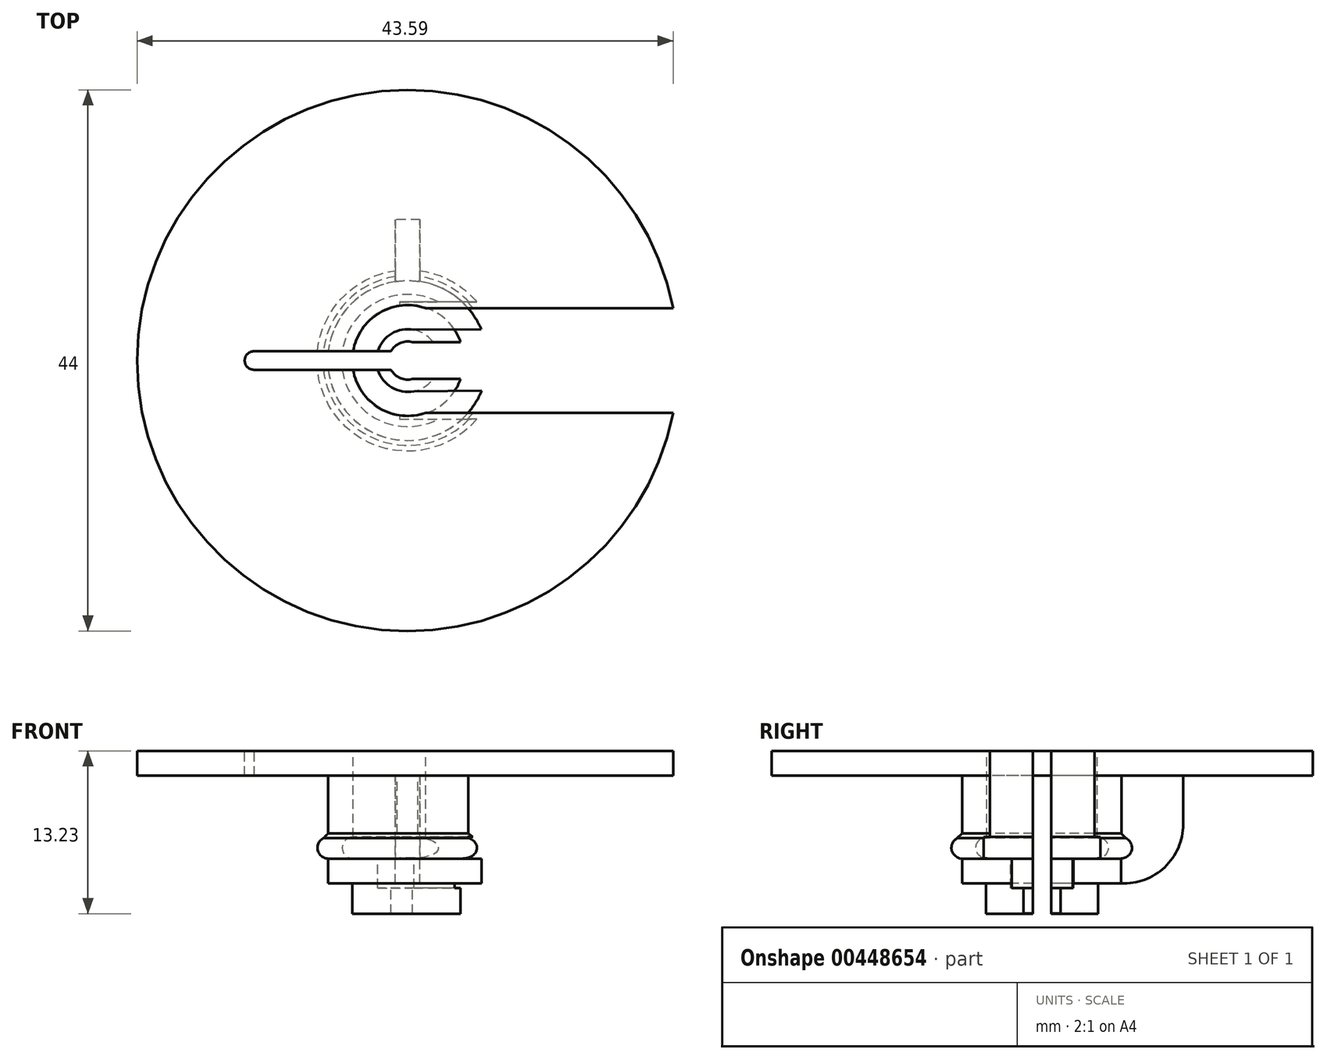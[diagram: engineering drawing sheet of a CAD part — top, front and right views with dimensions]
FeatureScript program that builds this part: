
annotation { "Feature Type Name" : "Feature", "Feature Type Description" : "" }
export const myFeature = defineFeature(function(context is Context, id is Id, definition is map)
    precondition{}
    {
        {
            var Q0;
            Q0=qCreatedBy(makeId("Front.planeOp"),FACE);
            var sketch = newSketch(context, id + "F0", { "sketchPlane" : qUnion([Q0])});
            skLineSegment(sketch, "E0", {"start": v(-22, -6) * mm, "end": v(-22, -8) * mm});
            skLineSegment(sketch, "E1", {"start": v(-22, -8) * mm, "end": v(-6.5, -8) * mm});
            skLineSegment(sketch, "E2", {"start": v(-6.5, -8) * mm, "end": v(-6.5, -12.7) * mm});
            skLineSegment(sketch, "E3", {"start": v(-6.5, -16.75) * mm, "end": v(-4.55, -16.75) * mm});
            skLineSegment(sketch, "E4", {"start": v(-4.55, -16.75) * mm, "end": v(-4.55, -19.23) * mm});
            skLineSegment(sketch, "E5", {"start": v(-22, -6) * mm, "end": v(-4.5, -6) * mm});
            skLineSegment(sketch, "E6", {"start": v(-4.5, -6) * mm, "end": v(-4.5, -13) * mm});
            skLineSegment(sketch, "E7", {"start": v(-4.5, -14.75) * mm, "end": v(-2.55, -14.75) * mm});
            skLineSegment(sketch, "E8", {"start": v(-2.55, -14.75) * mm, "end": v(-2.55, -17.15) * mm});
            skLineSegment(sketch, "E9", {"start": v(-2.55, -19.23) * mm, "end": v(-4.55, -19.23) * mm});
            skArc(sketch, "E10", {"start": v(-4.5, -13) * mm, "mid": v(-5.38, -13.88) * mm, "end": v(-4.5, -14.75) * mm});
            skArc(sketch, "E11", {"start": v(-6.9, -13.1) * mm, "mid": v(-7.35, -14.08) * mm, "end": v(-6.5, -14.75) * mm});
            skLineSegment(sketch, "E12.trimOffspring", {"start": v(-6.5, -14.75) * mm, "end": v(-6.5, -16.75) * mm});
            skLineSegment(sketch, "E13", {"start": v(0, -5.4) * mm, "end": v(0, -17.61) * mm, "construction": true});
            skLineSegment(sketch, "E14", {"start": v(-2.55, -17.15) * mm, "end": v(-1.55, -17.15) * mm});
            skLineSegment(sketch, "E15", {"start": v(-1.55, -17.15) * mm, "end": v(-1.55, -19.22) * mm});
            skLineSegment(sketch, "E16", {"start": v(-1.55, -19.22) * mm, "end": v(-2.55, -19.23) * mm});
            skPoint(sketch, "E17", {"position": v(-5.38, -13.88) * mm});
            skLineSegment(sketch, "E18", {"start": v(-6.9, -13.1) * mm, "end": v(-6.5, -12.7) * mm});
            skSolve(sketch);
        }
        {
            var Q0;
            Q0=makeQuery(id+"F0.imprint","IMPRINT",FACE,{"disambiguationData":[TD([[makeQuery(id+"F0.imprint","IMPRINT",EDGE,{"derivedFrom":sQuery(id+"F0.wireOp",EDGE,"E0")}),1.0]])]});
            var Q1;
            Q1=sQuery(id+"F0.wireOp",EDGE,"E13");
            revolve(context, id + "F1", {"entities" : qUnion([Q0]), "axis" : qUnion([Q1]), "revolveType" : RevolveType.FULL});
        }
        {
            var Q0;
            Q0=makeQuery(id+"F1.opRevolve","SWEPT_FACE",FACE,{"disambiguationData":[OSD([sQuery(id+"F0.wireOp",EDGE,"E5")])]});
            var sketch = newSketch(context, id + "F2", { "sketchPlane" : qUnion([Q0])});
            skLineSegment(sketch, "E19", {"start": v(-1.36, 0.75) * mm, "end": v(-12.48, 0.75) * mm});
            skLineSegment(sketch, "E20", {"start": v(-12.48, -0.75) * mm, "end": v(-1.36, -0.75) * mm});
            skArc(sketch, "E21", {"start": v(-1.36, 0.75) * mm, "mid": v(-1.55, 0) * mm, "end": v(-1.36, -0.75) * mm});
            skArc(sketch, "E22", {"start": v(-12.48, 0.75) * mm, "mid": v(-13.25, 0) * mm, "end": v(-12.48, -0.75) * mm});
            skSolve(sketch);
        }
        {
            var Q0;
            Q0 = qSketchRegion(id + "F2", true);
            extrude(context, id + "F3", {"entities" : qUnion([Q0]), "operationType" : NewBodyOperationType.REMOVE, "endBound" : BoundingType.SYMMETRIC, "oppositeDirection" : true, "depth" : 40 * mm});
        }
        {
            var Q0;
            Q0=makeQuery(id+"F1.opRevolve","SWEPT_FACE",FACE,{"disambiguationData":[OSD([sQuery(id+"F0.wireOp",EDGE,"E5")])]});
            var sketch = newSketch(context, id + "F4", { "sketchPlane" : qUnion([Q0])});
            skLineSegment(sketch, "E23", {"start": v(0, 4.25) * mm, "end": v(0, -4.25) * mm});
            skLineSegment(sketch, "E24", {"start": v(0, -4.25) * mm, "end": v(23.82, -4.25) * mm});
            skLineSegment(sketch, "E25", {"start": v(23.82, -4.25) * mm, "end": v(23.82, 4.25) * mm});
            skLineSegment(sketch, "E26", {"start": v(23.82, 4.25) * mm, "end": v(0, 4.25) * mm});
            skSolve(sketch);
        }
        {
            var Q0;
            Q0 = qSketchRegion(id + "F4", true);
            extrude(context, id + "F5", {"entities" : qUnion([Q0]), "operationType" : NewBodyOperationType.REMOVE, "oppositeDirection" : true, "depth" : 8.4 * mm});
        }
        {
            var Q0;
            {var subQ0=sQuery(id+"F4.wireOp",EDGE,"E24");var subQ2=sQuery(id+"F0.wireOp",EDGE,"E5");var subQ5=makeQuery(id+"F1.opRevolve","SWEPT_EDGE",EDGE,{"disambiguationData":[OSD([sQuery(id+"F0.wireOp",EDGE,"E0"),subQ2])]});var subQ6=makeQuery(id+"F4.imprint","INTERSECT",VERTEX,{"derivedFrom":[subQ5,subQ0]});Q0=makeQuery(id+"F4.imprint","IMPRINT",FACE,{"disambiguationData":[TD([[makeQuery(id+"F4.imprint","IMPRINT",EDGE,{"disambiguationData":[TD([[subQ6,1.0]])],"derivedFrom":subQ0}),1.0]])]});}
            cPlane(context, id + "F6", {"entities" : qUnion([Q0]), "cplaneType" : CPlaneType.OFFSET, "offset" : 8.75 * mm, "oppositeDirection" : true, "width" : 150 * mm, "height" : 150 * mm});
        }
        {
            var Q0;
            Q0=qCreatedBy(id+"F6.planeOp",FACE);
            var sketch = newSketch(context, id + "F7", { "sketchPlane" : qUnion([Q0])});
            skLineSegment(sketch, "E27", {"start": v(-0.66, 4.75) * mm, "end": v(-0.66, -4.75) * mm});
            skLineSegment(sketch, "E28", {"start": v(-0.66, -4.75) * mm, "end": v(24.48, -4.75) * mm});
            skLineSegment(sketch, "E29", {"start": v(24.48, -4.75) * mm, "end": v(24.48, 4.75) * mm});
            skLineSegment(sketch, "E30", {"start": v(24.48, 4.75) * mm, "end": v(-0.66, 4.75) * mm});
            skSolve(sketch);
        }
        {
            var Q0;
            Q0 = qSketchRegion(id + "F7", true);
            extrude(context, id + "F8", {"entities" : qUnion([Q0]), "operationType" : NewBodyOperationType.REMOVE, "depth" : 1.75 * mm});
        }
        {
            var Q0;
            Q0=makeQuery(id+"F8.boolean.opBoolean","MERGE",FACE,{"derivedFrom":[makeQuery(id+"F1.opRevolve","SWEPT_FACE",FACE,{"disambiguationData":[OSD([sQuery(id+"F0.wireOp",EDGE,"E7")])]}),makeQuery(id+"F8.opExtrude","CAP_FACE",FACE,{"disambiguationData":[OSD([sQuery(id+"F7.wireOp",EDGE,"E27"),sQuery(id+"F7.wireOp",EDGE,"E28"),sQuery(id+"F7.wireOp",EDGE,"E29"),sQuery(id+"F7.wireOp",EDGE,"E30")])],"isStart":true})]});
            var sketch = newSketch(context, id + "F9", { "sketchPlane" : qUnion([Q0])});
            skLineSegment(sketch, "E31", {"start": v(0.5, -2.5) * mm, "end": v(8, -2.44) * mm});
            skLineSegment(sketch, "E32", {"start": v(8, -2.44) * mm, "end": v(8, 2.56) * mm});
            skLineSegment(sketch, "E33", {"start": v(8, 2.56) * mm, "end": v(0.5, 2.5) * mm});
            skArc(sketch, "E34.0", {"start": v(0.5, -2.5) * mm, "mid": v(2.55, 0) * mm, "end": v(0.5, 2.5) * mm});
            skPoint(sketch, "E35.orphan", {"position": v(-2.44, 0.75) * mm});
            skPoint(sketch, "E36.orphan", {"position": v(-2.44, -0.75) * mm});
            skSolve(sketch);
        }
        {
            var Q0;
            Q0 = qSketchRegion(id + "F9", true);
            extrude(context, id + "F10", {"entities" : qUnion([Q0]), "operationType" : NewBodyOperationType.REMOVE, "oppositeDirection" : true, "depth" : 2.4 * mm});
        }
        {
            var Q0;
            Q0=makeQuery(id+"F10.boolean.opBoolean","MERGE",FACE,{"derivedFrom":[makeQuery(id+"F1.opRevolve","SWEPT_FACE",FACE,{"disambiguationData":[OSD([sQuery(id+"F0.wireOp",EDGE,"E14")])]}),makeQuery(id+"F10.opExtrude","CAP_FACE",FACE,{"disambiguationData":[OSD([sQuery(id+"F9.wireOp",EDGE,"E31"),sQuery(id+"F9.wireOp",EDGE,"E32"),sQuery(id+"F9.wireOp",EDGE,"E33"),sQuery(id+"F9.wireOp",EDGE,"E34.0")])],"isStart":false})]});
            var sketch = newSketch(context, id + "F11", { "sketchPlane" : qUnion([Q0])});
            skArc(sketch, "E37.0", {"start": v(-1.36, -0.75) * mm, "mid": v(1.55, 0) * mm, "end": v(-1.36, 0.75) * mm});
            skLineSegment(sketch, "E38", {"start": v(0.4, -1.5) * mm, "end": v(6.81, -1.5) * mm});
            skLineSegment(sketch, "E39", {"start": v(6.81, -1.5) * mm, "end": v(6.81, 1.5) * mm});
            skLineSegment(sketch, "E40", {"start": v(6.81, 1.5) * mm, "end": v(0.4, 1.5) * mm});
            skSolve(sketch);
        }
        {
            var Q0;
            Q0 = qSketchRegion(id + "F11", true);
            extrude(context, id + "F12", {"entities" : qUnion([Q0]), "operationType" : NewBodyOperationType.REMOVE, "oppositeDirection" : true, "depth" : 5 * mm});
        }
        {
            var Q0;
            Q0=qCreatedBy(makeId("Right.planeOp"),FACE);
            var sketch = newSketch(context, id + "F13", { "sketchPlane" : qUnion([Q0])});
            skLineSegment(sketch, "E41", {"start": v(11.47, -11.97) * mm, "end": v(11.47, -8) * mm});
            skLineSegment(sketch, "E42", {"start": v(11.47, -8) * mm, "end": v(6.45, -8) * mm});
            skLineSegment(sketch, "E43", {"start": v(6.45, -8) * mm, "end": v(6.45, -13) * mm});
            skLineSegment(sketch, "E44", {"start": v(6.38, -14.75) * mm, "end": v(6.38, -16.75) * mm});
            skArc(sketch, "E45", {"start": v(6.38, -14.75) * mm, "mid": v(7.28, -13.91) * mm, "end": v(6.45, -13) * mm});
            skLineSegment(sketch, "E46", {"start": v(6.45, -8) * mm, "end": v(11.47, -8) * mm, "construction": true});
            skArc(sketch, "E47", {"start": v(6.38, -16.75) * mm, "mid": v(9.96, -15.47) * mm, "end": v(11.47, -11.97) * mm});
            skArc(sketch, "E48.MirrorCS", {"start": v(-6.38, -14.75) * mm, "mid": v(-7.28, -13.91) * mm, "end": v(-6.45, -13) * mm});
            skArc(sketch, "E49.MirrorCS", {"start": v(-6.38, -16.75) * mm, "mid": v(-9.96, -15.47) * mm, "end": v(-11.47, -11.97) * mm});
            skLineSegment(sketch, "E50.MirrorCS", {"start": v(-11.47, -11.97) * mm, "end": v(-11.47, -8) * mm});
            skLineSegment(sketch, "E51.MirrorCS", {"start": v(-6.45, -8) * mm, "end": v(-6.45, -13) * mm});
            skLineSegment(sketch, "E52.MirrorCS", {"start": v(-6.38, -14.75) * mm, "end": v(-6.38, -16.75) * mm});
            skLineSegment(sketch, "E53", {"start": v(-11.47, -8) * mm, "end": v(-6.45, -8) * mm});
            skSolve(sketch);
        }
        {
            var Q0;
            Q0=makeQuery(id+"F13.imprint","IMPRINT",FACE,{"disambiguationData":[TD([[makeQuery(id+"F13.imprint","IMPRINT",EDGE,{"derivedFrom":sQuery(id+"F13.wireOp",EDGE,"E41")}),1.0]])]});
            var Q1;
            {var subQ1=sQuery(id+"F13.wireOp",EDGE,"E48.MirrorCS");Q1=makeQuery(id+"F13.imprint","IMPRINT",FACE,{"disambiguationData":[TD([[makeQuery(id+"F13.imprint","IMPRINT",EDGE,{"derivedFrom":subQ1}),1.0]])]});}
            extrude(context, id + "F14", {"entities" : qUnion([Q0, Q1]), "operationType" : NewBodyOperationType.ADD, "endBound" : BoundingType.SYMMETRIC, "depth" : 2 * mm});
        }
    });
